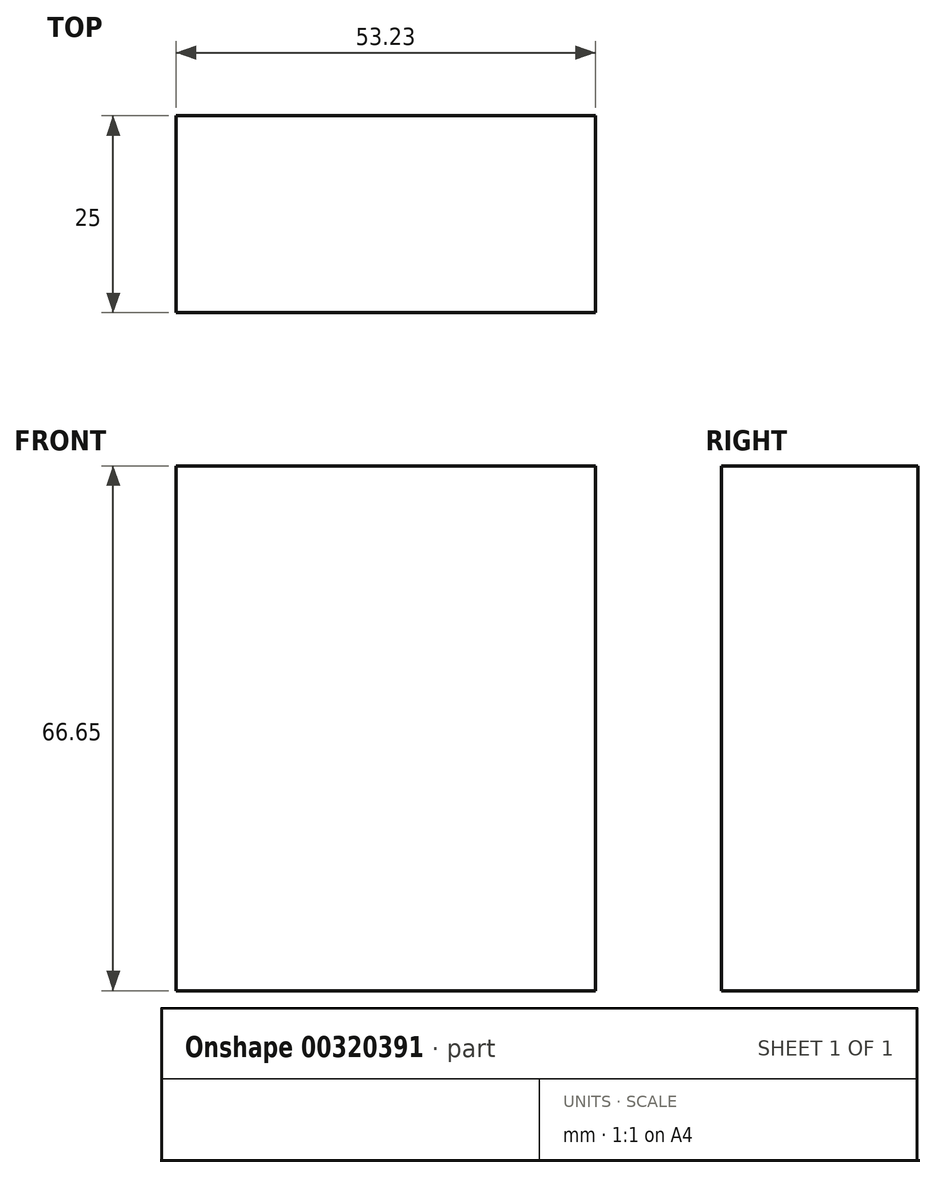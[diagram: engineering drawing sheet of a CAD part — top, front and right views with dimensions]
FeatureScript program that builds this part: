
annotation { "Feature Type Name" : "Feature", "Feature Type Description" : "" }
export const myFeature = defineFeature(function(context is Context, id is Id, definition is map)
    precondition{}
    {
        {
            var Q0;
            Q0=qCreatedBy(makeId("Front.planeOp"),FACE);
            var sketch = newSketch(context, id + "F0", { "sketchPlane" : qUnion([Q0])});
            skLineSegment(sketch, "E0.bottom", {"start": v(-95.42, -5.48) * mm, "end": v(-42.2, -5.48) * mm});
            skLineSegment(sketch, "E0.top", {"start": v(-95.42, 61.17) * mm, "end": v(-42.2, 61.17) * mm});
            skLineSegment(sketch, "E0.left", {"start": v(-95.42, -5.48) * mm, "end": v(-95.42, 61.17) * mm});
            skLineSegment(sketch, "E0.right", {"start": v(-42.2, -5.48) * mm, "end": v(-42.2, 61.17) * mm});
            skPoint(sketch, "E0.middle", {"position": v(-68.8, 27.85) * mm});
            skSolve(sketch);
        }
        {
            var Q0;
            Q0=makeQuery(id+"F0.imprint","IMPRINT",FACE,{"disambiguationData":[TD([[makeQuery(id+"F0.imprint","IMPRINT",EDGE,{"derivedFrom":sQuery(id+"F0.wireOp",EDGE,"E0.bottom")}),1.0]])]});
            extrude(context, id + "F1", {"entities" : qUnion([Q0]), "depth" : 25 * mm});
        }
    });
